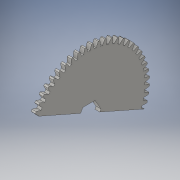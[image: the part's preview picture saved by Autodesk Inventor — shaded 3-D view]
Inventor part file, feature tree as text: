
AUTODESK INVENTOR PART (.ipt)
format: ipt  version: 2016 (Build 200138000, 138)  size: 460,800 bytes
history: native  units: in
note: dims shown in document units (in); Inventor stores cm internally (conversion verified against a paired STEP export)
features: extrude x3, sketch x3, chamfer x1
ambient origin geometry x8: Origin, YZ Plane, XZ Plane, XY Plane, X Axis, Y Axis, Z Axis, Center Point
bodies: Solid1 (feature_tree)
feature tree (7):
  extrude  "Extrusion1"  Depth=1.0in TaperAngle=0.0deg
  extrude  "Extrusion2"  [1 undecoded]
  extrude  "Extrusion3"  [1 undecoded]
  sketch  "Sketch1"  dims[d0=1.0in d1=0.0in d2=1.0in d3=0.0in]
  sketch  "Sketch2"  dims[d4=3.0in d5=0.0in]
  sketch  "Sketch3"
  chamfer  "Chamfer2"  [1 undecoded]
note: 3 required parameter values undecoded (feature->parameter linkage not recoverable at this tier; creation-order binding heuristic only, values carry confidence <= 0.55)
